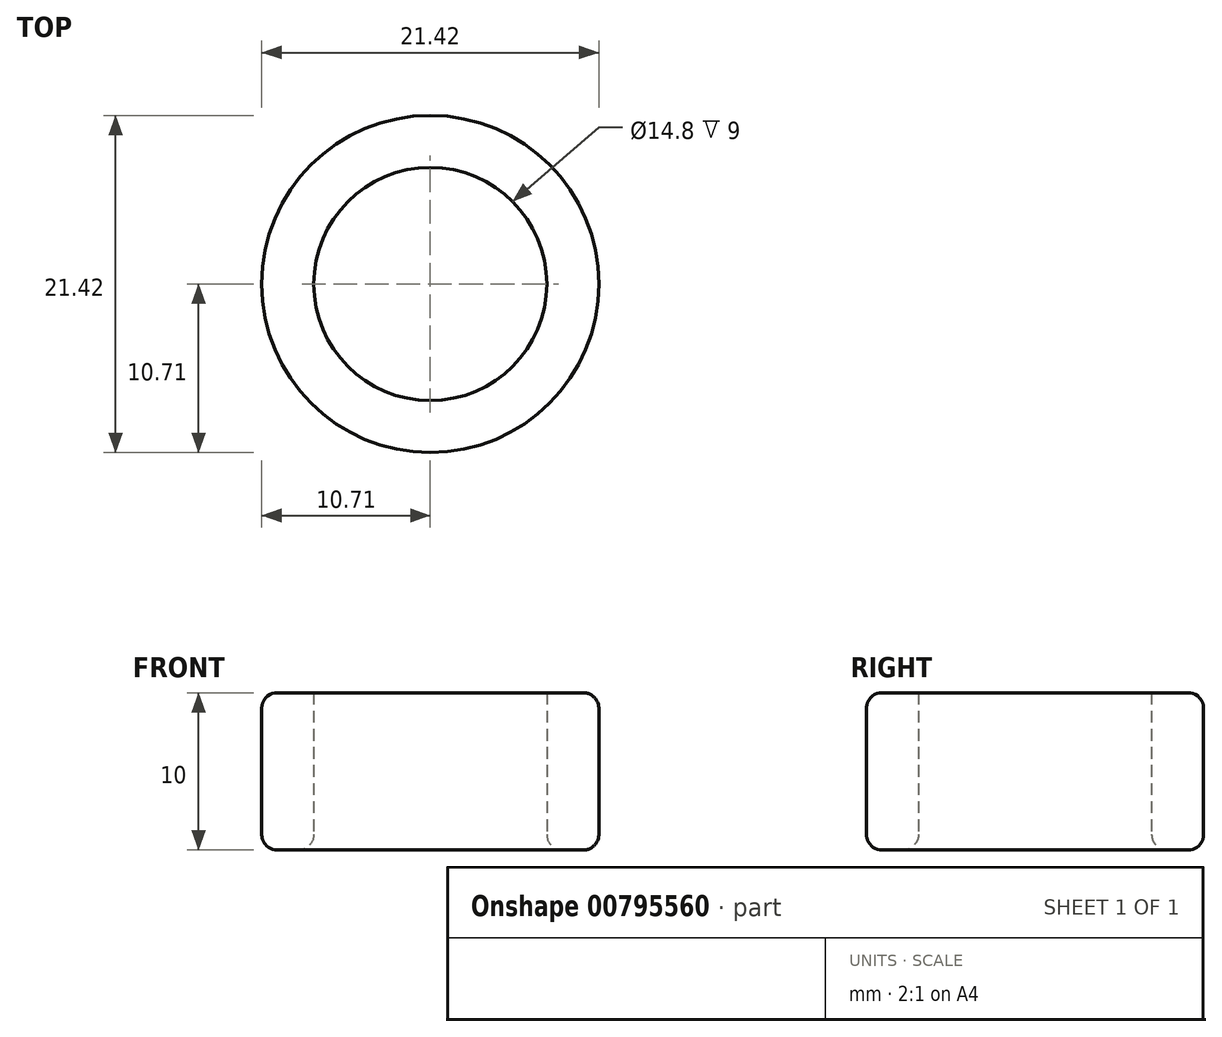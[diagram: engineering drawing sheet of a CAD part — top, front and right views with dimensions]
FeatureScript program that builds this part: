
annotation { "Feature Type Name" : "Feature", "Feature Type Description" : "" }
export const myFeature = defineFeature(function(context is Context, id is Id, definition is map)
    precondition{}
    {
        {
            var Q0;
            Q0=qCreatedBy(makeId("Top.planeOp"),FACE);
            var sketch = newSketch(context, id + "F0", { "sketchPlane" : qUnion([Q0])});
            skCircle(sketch, "E0", {"center": v(0, 0) * mm, "radius": 7.4 * mm});
            skCircle(sketch, "E1", {"center": v(0, 0) * mm, "radius": 10.7 * mm});
            skSolve(sketch);
        }
        {
            var Q0;
            Q0=makeQuery(id+"F0.imprint","IMPRINT",FACE,{"disambiguationData":[TD([[makeQuery(id+"F0.imprint","IMPRINT",EDGE,{"derivedFrom":sQuery(id+"F0.wireOp",EDGE,"E0")}),-1.0]])]});
            extrude(context, id + "F1", {"entities" : qUnion([Q0]), "depth" : 10 * mm, "offsetDistance" : 25.4 * mm});
        }
        {
            var Q0;
            Q0=makeQuery(id+"F1.opExtrude","CAP_EDGE",EDGE,{"disambiguationData":[OSD([sQuery(id+"F0.wireOp",EDGE,"E1")])],"isStart":false});
            var Q1;
            Q1=makeQuery(id+"F1.opExtrude","CAP_FACE",FACE,{"disambiguationData":[OSD([sQuery(id+"F0.wireOp",EDGE,"E0"),sQuery(id+"F0.wireOp",EDGE,"E1")])],"isStart":true});
            fillet(context, id + "F2", {"entities" : qUnion([Q0, Q1]), "radius" : 1 * mm, "tangentPropagation" : true, "allowEdgeOverflow" : false});
        }
    });
